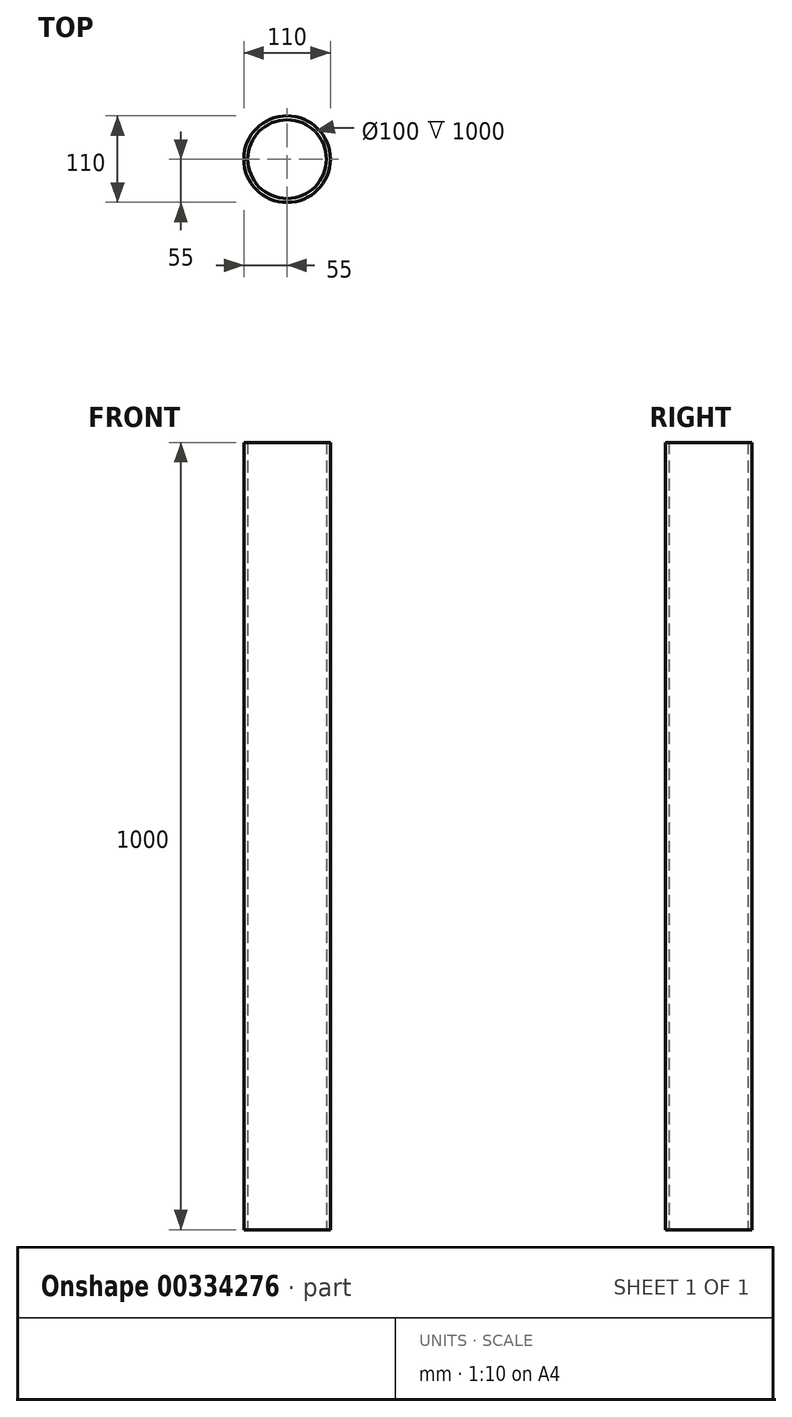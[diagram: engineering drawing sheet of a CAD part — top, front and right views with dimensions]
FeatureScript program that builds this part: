
annotation { "Feature Type Name" : "Feature", "Feature Type Description" : "" }
export const myFeature = defineFeature(function(context is Context, id is Id, definition is map)
    precondition{}
    {
        {
            var Q0;
            Q0=qCreatedBy(makeId("Top.planeOp"),FACE);
            var sketch = newSketch(context, id + "F0", { "sketchPlane" : qUnion([Q0])});
            skCircle(sketch, "E0", {"center": v(0, 0) * mm, "radius": 50 * mm});
            skCircle(sketch, "E1", {"center": v(0, 0) * mm, "radius": 55 * mm});
            skSolve(sketch);
        }
        {
            var Q0;
            Q0=makeQuery(id+"F0.imprint","IMPRINT",FACE,{"disambiguationData":[TD([[makeQuery(id+"F0.imprint","IMPRINT",EDGE,{"derivedFrom":sQuery(id+"F0.wireOp",EDGE,"E0")}),-1.0]])]});
            extrude(context, id + "F1", {"entities" : qUnion([Q0]), "depth" : 1000 * mm});
        }
    });
